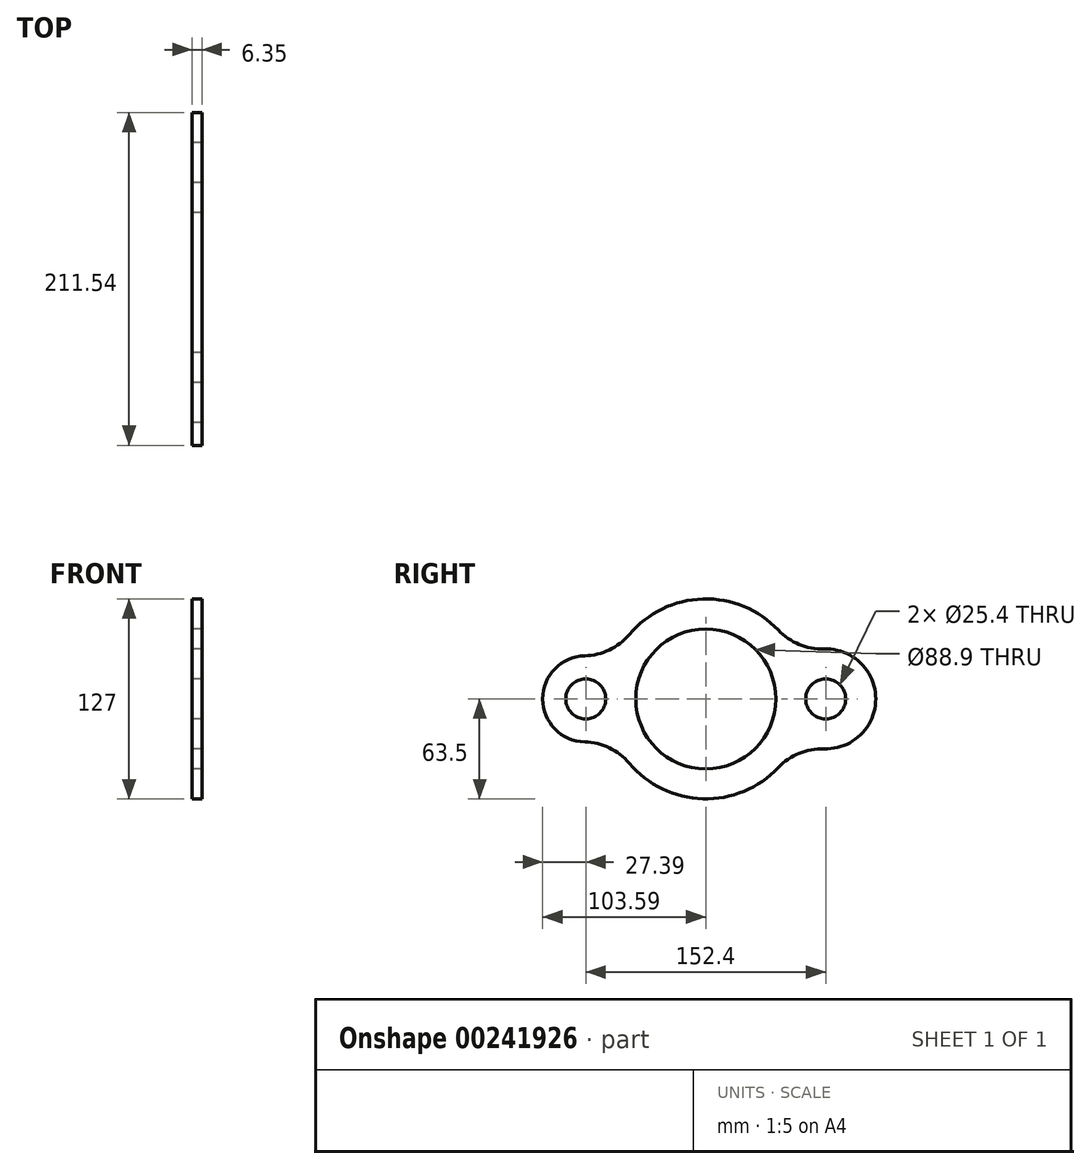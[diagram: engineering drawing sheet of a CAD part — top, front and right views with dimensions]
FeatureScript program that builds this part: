
annotation { "Feature Type Name" : "Feature", "Feature Type Description" : "" }
export const myFeature = defineFeature(function(context is Context, id is Id, definition is map)
    precondition{}
    {
        {
            var Q0;
            Q0=qCreatedBy(makeId("Right.planeOp"),FACE);
            var sketch = newSketch(context, id + "F0", { "sketchPlane" : qUnion([Q0])});
            skCircle(sketch, "E0", {"center": v(0, 0) * mm, "radius": 44.45 * mm});
            skArc(sketch, "E1", {"start": v(-48.56, -40.92) * mm, "mid": v(-1.82, -63.47) * mm, "end": v(46.14, -43.63) * mm});
            skArc(sketch, "E2", {"start": v(75.12, -31.73) * mm, "mid": v(107.95, 0) * mm, "end": v(75.12, 31.73) * mm});
            skArc(sketch, "E3", {"start": v(-76.82, 27.38) * mm, "mid": v(-103.59, 0) * mm, "end": v(-76.82, -27.38) * mm});
            skCircle(sketch, "E4", {"center": v(76.2, 0) * mm, "radius": 12.7 * mm});
            skCircle(sketch, "E5", {"center": v(-76.2, 0) * mm, "radius": 12.7 * mm});
            skArc(sketch, "E6.trimOffspring", {"start": v(46.14, 43.63) * mm, "mid": v(-1.82, 63.47) * mm, "end": v(-48.56, 40.92) * mm});
            skPoint(sketch, "E7.visualSharp", {"position": v(-59.64, 21.8) * mm});
            skArc(sketch, "E7.filletArc", {"start": v(-76.82, 27.38) * mm, "mid": v(-61.24, 31.1) * mm, "end": v(-48.56, 40.92) * mm});
            skPoint(sketch, "E8.visualSharp", {"position": v(57.94, 25.98) * mm});
            skArc(sketch, "E8.filletArc", {"start": v(46.14, 43.63) * mm, "mid": v(59.35, 34.56) * mm, "end": v(75.12, 31.73) * mm});
            skPoint(sketch, "E9.visualSharp", {"position": v(57.94, -25.98) * mm});
            skArc(sketch, "E9.filletArc", {"start": v(75.12, -31.73) * mm, "mid": v(59.35, -34.56) * mm, "end": v(46.14, -43.63) * mm});
            skPoint(sketch, "E10.visualSharp", {"position": v(-59.64, -21.8) * mm});
            skArc(sketch, "E10.filletArc", {"start": v(-48.56, -40.92) * mm, "mid": v(-61.24, -31.1) * mm, "end": v(-76.82, -27.38) * mm});
            skSolve(sketch);
        }
        {
            var Q0;
            Q0 = qSketchRegion(id + "F0", true);
            extrude(context, id + "F1", {"entities" : qUnion([Q0]), "depth" : 6.35 * mm});
        }
    });
